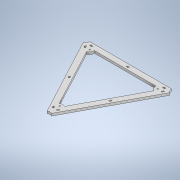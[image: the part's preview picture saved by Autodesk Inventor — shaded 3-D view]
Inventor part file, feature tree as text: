
AUTODESK INVENTOR PART (.ipt)
format: ipt  version: 2020 (Build 240168000, 168)  size: 169,472 bytes
history: native  units: in
note: dims shown in document units (in); Inventor stores cm internally (conversion verified against a paired STEP export)
features: extrude x1, sketch x1
ambient origin geometry x8: Origin, YZ Plane, XZ Plane, XY Plane, X Axis, Y Axis, Z Axis, Center Point
bodies: Solid1 (feature_tree)
feature tree (2):
  extrude  "Extrusion1"  [1 undecoded]
  sketch  "Sketch1"  dims[d0=0.1575in d1=0.0in]
note: 1 required parameter value undecoded (feature->parameter linkage not recoverable at this tier; creation-order binding heuristic only, values carry confidence <= 0.55)
